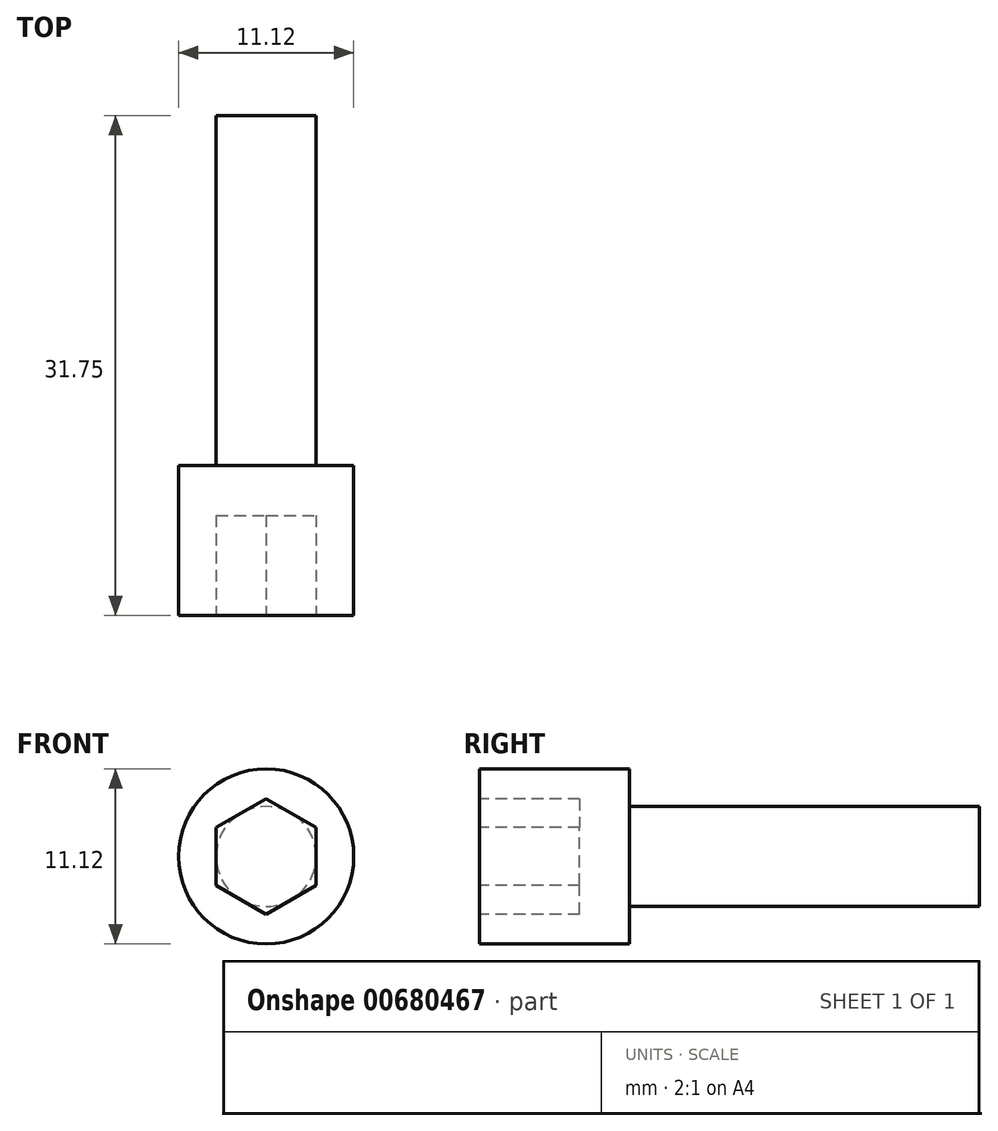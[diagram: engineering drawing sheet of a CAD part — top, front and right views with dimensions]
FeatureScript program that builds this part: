
annotation { "Feature Type Name" : "Feature", "Feature Type Description" : "" }
export const myFeature = defineFeature(function(context is Context, id is Id, definition is map)
    precondition{}
    {
        {
            var Q0;
            Q0=qCreatedBy(makeId("Front.planeOp"),FACE);
            var sketch = newSketch(context, id + "F0", { "sketchPlane" : qUnion([Q0])});
            skCircle(sketch, "E0", {"center": v(0, 0) * mm, "radius": 3.18 * mm});
            skSolve(sketch);
        }
        {
            var Q0;
            Q0=makeQuery(id+"F0.imprint","IMPRINT",FACE,{"disambiguationData":[TD([[makeQuery(id+"F0.imprint","IMPRINT",EDGE,{"derivedFrom":sQuery(id+"F0.wireOp",EDGE,"E0")}),1.0]])]});
            extrude(context, id + "F1", {"entities" : qUnion([Q0]), "depth" : 22.22 * mm, "offsetDistance" : 25.4 * mm});
        }
        {
            var Q0;
            Q0=makeQuery(id+"F1.opExtrude","CAP_FACE",FACE,{"disambiguationData":[OSD([sQuery(id+"F0.wireOp",EDGE,"E0")])],"isStart":false});
            var sketch = newSketch(context, id + "F2", { "sketchPlane" : qUnion([Q0])});
            skCircle(sketch, "E1.cCircle", {"center": v(0, 0) * mm, "radius": 5.56 * mm, "construction": true});
            skLineSegment(sketch, "E1.0", {"start": v(0, 6.42) * mm, "end": v(5.56, 3.21) * mm});
            skLineSegment(sketch, "E1.1", {"start": v(5.56, 3.21) * mm, "end": v(5.56, -3.21) * mm});
            skLineSegment(sketch, "E1.2", {"start": v(5.56, -3.21) * mm, "end": v(0, -6.42) * mm});
            skLineSegment(sketch, "E1.3", {"start": v(0, -6.42) * mm, "end": v(-5.56, -3.21) * mm});
            skLineSegment(sketch, "E1.4", {"start": v(-5.56, -3.21) * mm, "end": v(-5.56, 3.21) * mm});
            skLineSegment(sketch, "E1.5", {"start": v(-5.56, 3.21) * mm, "end": v(0, 6.42) * mm});
            skPoint(sketch, "E1.0.midPoint", {"position": v(2.78, 4.82) * mm});
            skSolve(sketch);
        }
        {
            var Q0;
            Q0=makeQuery(id+"F2.imprint","IMPRINT",FACE,{"disambiguationData":[TD([[makeQuery(id+"F2.imprint","IMPRINT",EDGE,{"derivedFrom":makeQuery(id+"F1.opExtrude","CAP_EDGE",EDGE,{"disambiguationData":[OSD([sQuery(id+"F0.wireOp",EDGE,"E0")])],"isStart":false})}),1.0]])]});
            var sketch = newSketch(context, id + "F3", { "sketchPlane" : qUnion([Q0])});
            skCircle(sketch, "E2.0", {"center": v(0, 0) * mm, "radius": 5.56 * mm});
            skSolve(sketch);
        }
        {
            var Q0;
            Q0 = qSketchRegion(id + "F3", true);
            extrude(context, id + "F4", {"entities" : qUnion([Q0]), "operationType" : NewBodyOperationType.ADD, "depth" : 9.52 * mm, "offsetDistance" : 25.4 * mm});
        }
        {
            var Q0;
            Q0=makeQuery(id+"F4.opExtrude","CAP_FACE",FACE,{"disambiguationData":[OSD([sQuery(id+"F3.wireOp",EDGE,"E2.0")])],"isStart":false});
            var sketch = newSketch(context, id + "F5", { "sketchPlane" : qUnion([Q0])});
            skCircle(sketch, "E3.cCircle", {"center": v(0, 0) * mm, "radius": 3.18 * mm, "construction": true});
            skLineSegment(sketch, "E3.0", {"start": v(0, 3.67) * mm, "end": v(3.17, 1.83) * mm});
            skLineSegment(sketch, "E3.1", {"start": v(3.17, 1.83) * mm, "end": v(3.17, -1.83) * mm});
            skLineSegment(sketch, "E3.2", {"start": v(3.17, -1.83) * mm, "end": v(0, -3.67) * mm});
            skLineSegment(sketch, "E3.3", {"start": v(0, -3.67) * mm, "end": v(-3.17, -1.83) * mm});
            skLineSegment(sketch, "E3.4", {"start": v(-3.17, -1.83) * mm, "end": v(-3.17, 1.83) * mm});
            skLineSegment(sketch, "E3.5", {"start": v(-3.17, 1.83) * mm, "end": v(0, 3.67) * mm});
            skPoint(sketch, "E3.0.midPoint", {"position": v(1.59, 2.75) * mm});
            skSolve(sketch);
        }
        {
            var Q0;
            Q0=makeQuery(id+"F5.imprint","IMPRINT",FACE,{"disambiguationData":[TD([[makeQuery(id+"F5.imprint","IMPRINT",EDGE,{"derivedFrom":sQuery(id+"F5.wireOp",EDGE,"E3.0")}),-1.0]])]});
            extrude(context, id + "F6", {"entities" : qUnion([Q0]), "operationType" : NewBodyOperationType.REMOVE, "oppositeDirection" : true, "depth" : 6.35 * mm, "offsetDistance" : 25.4 * mm});
        }
    });
